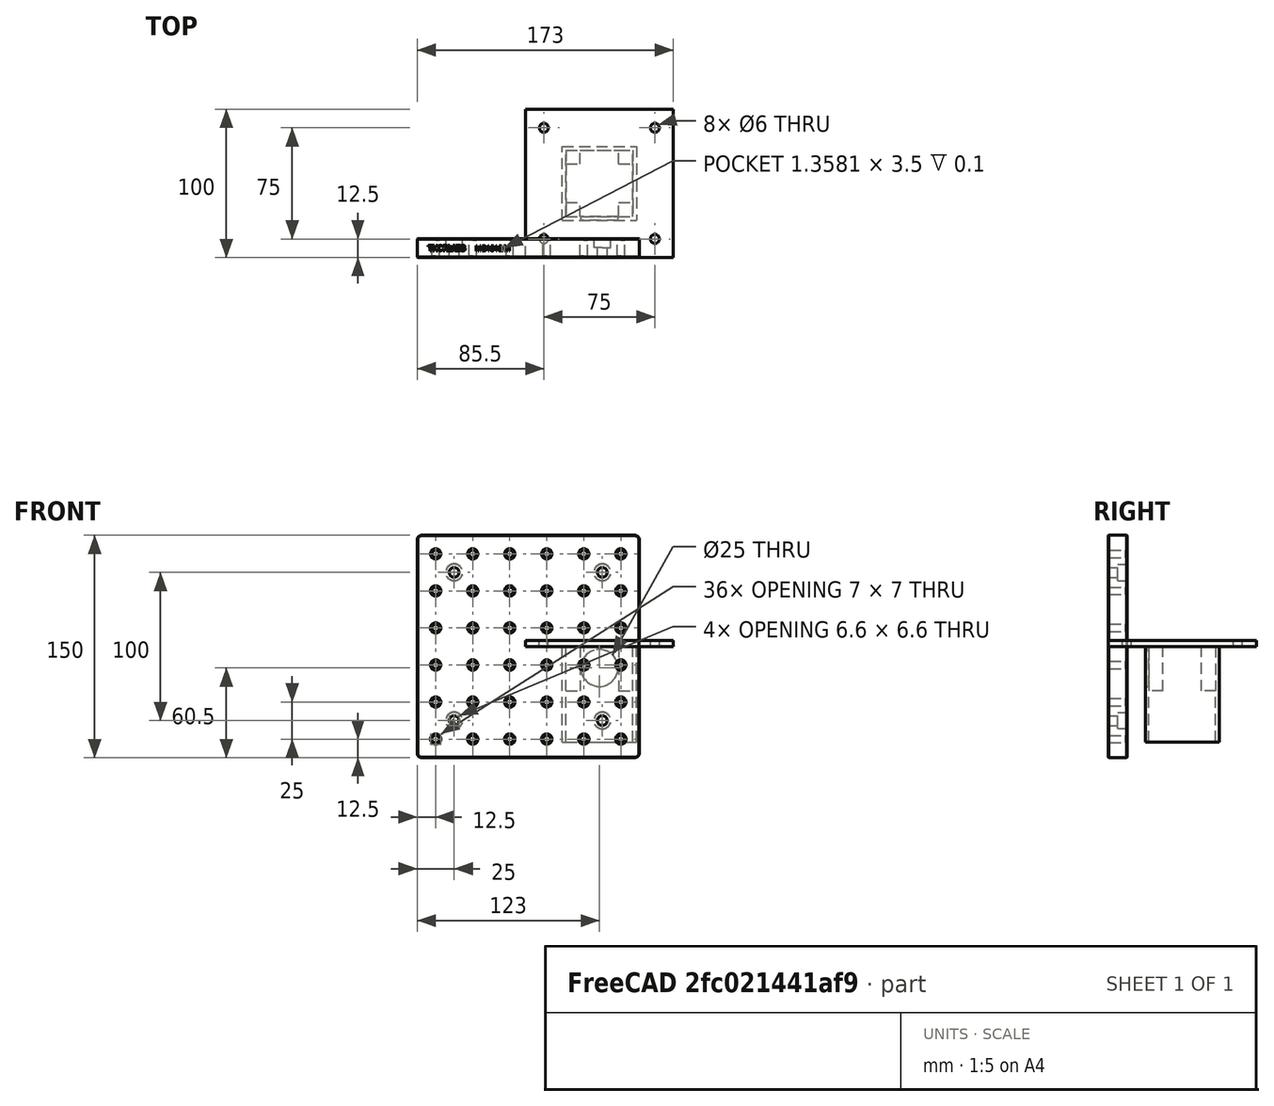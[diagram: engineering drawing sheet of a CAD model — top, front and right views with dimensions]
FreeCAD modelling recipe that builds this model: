
FCSTD DOCUMENT  (FreeCAD 0.21R33694 (Git))
Label: camera_box_v3
License: All rights reserved
LicenseURL: https://en.wikipedia.org/wiki/All_rights_reserved
objects: Part::Box×7, Part::Feature×5, Part::MultiFuse×3, Part::Cut×3, Part::Cylinder×1, App::Part×1
note: 19 computed .brp shape members not serialized (recipe doc carries the construction recipe); baked Part::Feature solids carry a one-line shape summary decoded from their .brp

FEATURE [Part::Box] Box  label="Cube"
  AttacherType = Attacher::AttachEngine3D
  Height = 4
  Length = 100
  Width = 100
FEATURE [Part::Box] Box001  label="Cube001"
  AttacherType = Attacher::AttachEngine3D
  Height = 65
  Length = 50
  Placement = pos=(22.5,22.5,-57) rot=(0,0,1;0rad)
  Width = 50
FEATURE [Part::Box] Box002  label="Cube002"
  AttacherType = Attacher::AttachEngine3D
  Height = 65
  Length = 45
  Placement = pos=(25,25,-57) rot=(0,0,1;0rad)
  Width = 45
FEATURE [Part::Box] Box003  label="Cube003"
  AttacherType = Attacher::AttachEngine3D
  Height = 30
  Length = 10
  Placement = pos=(27,27,-30) rot=(0,0,1;0rad)
  Width = 10
FEATURE [Part::Box] Box004  label="Cube004"
  AttacherType = Attacher::AttachEngine3D
  Height = 30
  Length = 10
  Placement = pos=(27,63,-30) rot=(0,0,1;0rad)
  Width = 10
FEATURE [Part::Box] Box005  label="Cube005"
  AttacherType = Attacher::AttachEngine3D
  Height = 30
  Length = 10
  Placement = pos=(63,63,-30) rot=(0,0,1;0rad)
  Width = 10
FEATURE [Part::Box] Box006  label="Cube006"
  AttacherType = Attacher::AttachEngine3D
  Height = 30
  Length = 10
  Placement = pos=(63,27,-30) rot=(0,0,1;0rad)
  Width = 10
FEATURE [Part::Cylinder] Cylinder
  Angle = 360
  AttacherType = Attacher::AttachEngine3D
  FirstAngle = 0
  Height = 5
  Placement = pos=(50,28.5,-7) rot=(1,0,0;1.5708rad)
  Radius = 12.5
  SecondAngle = 0
FEATURE [Part::Feature] Part__Feature  label="MB1515_M - Aluminium Breadboard 150 x 150 x 12.7mm_MB3030_M-1"
  Placement = pos=(2,0,0) rot=(0,0,1;0rad)
  shape: bbox 150 x 12.7 x 150 mm, 538 faces (baked)
FEATURE [App::Part] MB1515_M
  Group = -> [Part__Feature]
  Origin = -> Origin
  Placement = pos=(48,50,50) rot=(1,0,0;1.5708rad)
FEATURE [Part::Feature] BOLTS_part002  label="Hexagon head bolt M6 - 20.0"
  Placement = pos=(12.5,12.5,-4.05) rot=(0,0,1;0rad)
  shape: bbox 10 x 11.55 x 24 mm, 11 faces (baked)
FEATURE [Part::Feature] BOLTS_part003  label="Hexagon head bolt M6 - 20.001"
  Placement = pos=(12.5,87.5,-4.05) rot=(0,0,1;0rad)
  shape: bbox 10 x 11.55 x 24 mm, 11 faces (baked)
FEATURE [Part::Feature] BOLTS_part004  label="Hexagon head bolt M6 - 20.002"
  Placement = pos=(87.5,12.5,-4.05) rot=(0,0,1;0rad)
  shape: bbox 10 x 11.55 x 24 mm, 11 faces (baked)
FEATURE [Part::Feature] BOLTS_part005  label="Hexagon head bolt M6 - 20.003"
  Placement = pos=(87.5,87.5,-4.05) rot=(0,0,1;0rad)
  shape: bbox 10 x 11.55 x 24 mm, 11 faces (baked)
FEATURE [Part::MultiFuse] Fusion
  Shapes = -> [BOLTS_part002,BOLTS_part003,BOLTS_part004,BOLTS_part005]
FEATURE [Part::Cut] Cut002
  Base = -> Box
  Tool = -> Fusion
FEATURE [Part::Cut] Cut
  Base = -> Box001
  Placement = pos=(2.5,2.5,0) rot=(0,0,1;0rad)
  Tool = -> Box002
FEATURE [Part::Cut] Cut001
  Base = -> Cut
  Placement = pos=(0,0,-7.5) rot=(0,0,1;0rad)
  Tool = -> Cylinder
FEATURE [Part::MultiFuse] Fusion001
  Shapes = -> [Box003,Box004,Box005,Box006,Cut002]
FEATURE [Part::MultiFuse] Fusion002
  Shapes = -> [Cut001,Fusion001]
